# Revit family: 202_KSUN
name_source: partatom
category: Air Terminals
revit_build: Autodesk Revit 2018 (Build: 20170223_1515(x64)
units: mm (PartAtom-declared; Revit-internal decimal feet)

## family parameters
Always vertical = Yes
Cut with Voids When Loaded = No
Part Type = Normal
Room Calculation Point = Yes
Round Connector Dimension = Use Diameter
Shared = No
Work Plane-Based = No

## types (2) — shared parameters
CL_Location_5000 = 5000 mm  [stored 16.4042 ft]
Description = Extract valve steel white
H3 = 18 mm  [stored 0.0590551 ft]
H3__ve = -18 mm  [stored -0.0590551 ft]
L_ARR = 400 mm  [stored 1.31234 ft]
Manufacturer = Flexit
QmdConnectorList = 201;D
R4 = 54 mm  [stored 0.177165 ft]
URL = www.flexit.no
W_ARR = 400 mm  [stored 1.31234 ft]
magiPartTypeId = 202
magiProductFamilyId = KSUN
zero-valued in all types: CLBTZ, H_ARR

## per-type parameters (varying)
| type | D | H2 | R3 | R5 | magiProductId |
| 100-116457 | 100 mm | 32 mm  [stored 0.104987 ft] | 65 mm  [stored 0.213255 ft] | 38 mm | KSU 100N |
| 125-116458 | 125 mm | 50 mm  [stored 0.164042 ft] | 79 mm  [stored 0.259186 ft] | 51 mm | KSU 125N |

note: column(s) folded — value = type name in every type: MC Product Code

note: [stored X ft] marks values corroborated as IEEE doubles in the binary element streams (Revit-internal decimal feet)

## geometry (parser evidence)
native form markers: Sweep x1
no freeform markers — native parametric forms only
